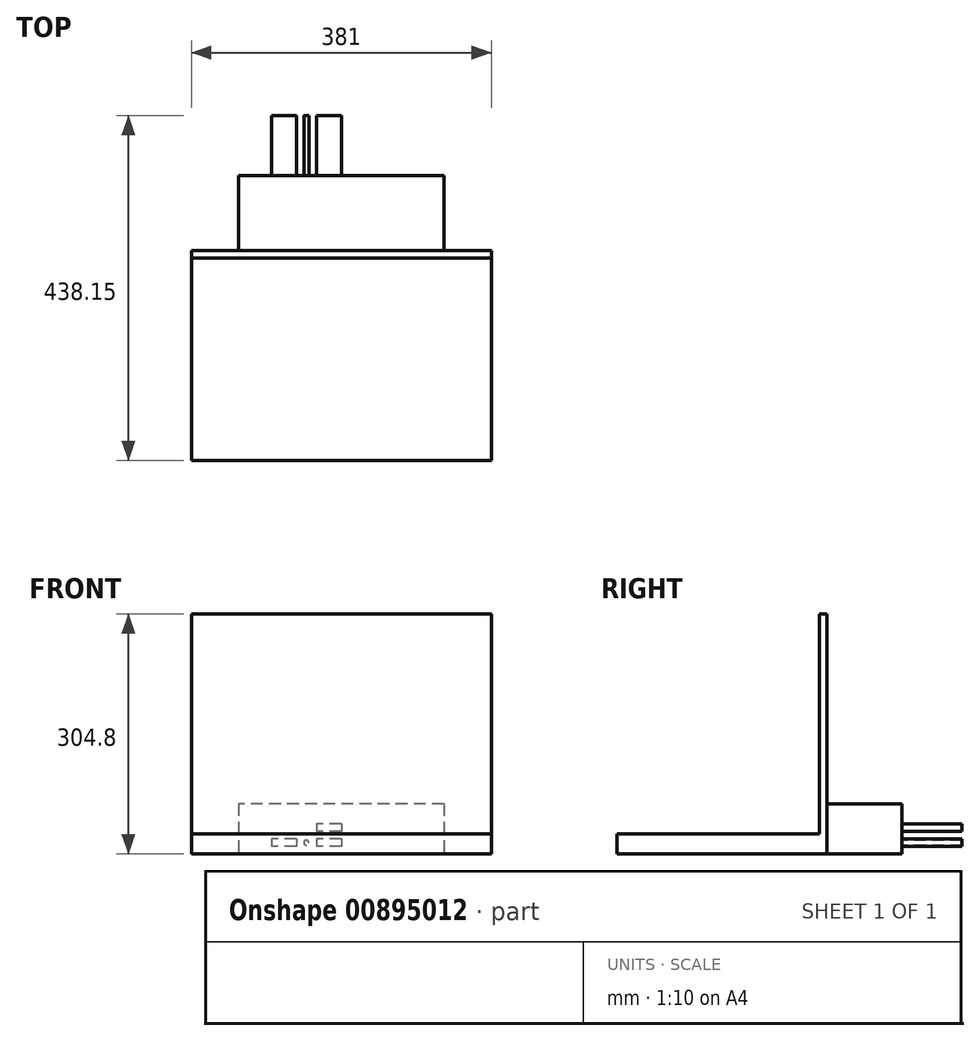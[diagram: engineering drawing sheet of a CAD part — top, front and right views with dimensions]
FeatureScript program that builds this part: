
annotation { "Feature Type Name" : "Feature", "Feature Type Description" : "" }
export const myFeature = defineFeature(function(context is Context, id is Id, definition is map)
    precondition{}
    {
        {
            var Q0;
            Q0=qCreatedBy(makeId("Right.planeOp"),FACE);
            var sketch = newSketch(context, id + "F0", { "sketchPlane" : qUnion([Q0])});
            skLineSegment(sketch, "E0", {"start": v(-266.7, 0) * mm, "end": v(0, 0) * mm});
            skLineSegment(sketch, "E1", {"start": v(0, 0) * mm, "end": v(0, 304.8) * mm});
            skLineSegment(sketch, "E2", {"start": v(0, 304.8) * mm, "end": v(-9.52, 304.8) * mm});
            skLineSegment(sketch, "E3", {"start": v(-9.52, 304.8) * mm, "end": v(-9.52, 25.4) * mm});
            skLineSegment(sketch, "E4", {"start": v(-9.52, 25.4) * mm, "end": v(-266.7, 25.4) * mm});
            skLineSegment(sketch, "E5", {"start": v(-266.7, 25.4) * mm, "end": v(-266.7, 0) * mm});
            skSolve(sketch);
        }
        {
            var Q0;
            Q0 = qSketchRegion(id + "F0", true);
            extrude(context, id + "F1", {"entities" : qUnion([Q0]), "depth" : 381 * mm, "offsetDistance" : 25.4 * mm, "symmetric" : true});
        }
        {
            var Q0;
            Q0=makeQuery(id+"F1.opExtrude","SWEPT_FACE",FACE,{"disambiguationData":[OSD([sQuery(id+"F0.wireOp",EDGE,"E1")])]});
            var sketch = newSketch(context, id + "F2", { "sketchPlane" : qUnion([Q0])});
            skLineSegment(sketch, "E6.bottom", {"start": v(-130.18, 63.5) * mm, "end": v(130.18, 63.5) * mm});
            skLineSegment(sketch, "E6.top", {"start": v(-130.17, 0) * mm, "end": v(130.18, 0) * mm});
            skLineSegment(sketch, "E6.left", {"start": v(-130.18, 63.5) * mm, "end": v(-130.18, 0) * mm});
            skLineSegment(sketch, "E6.right", {"start": v(130.18, 63.5) * mm, "end": v(130.18, 0) * mm});
            skSolve(sketch);
        }
        {
            var Q0;
            Q0 = qSketchRegion(id + "F2", true);
            extrude(context, id + "F3", {"entities" : qUnion([Q0]), "operationType" : NewBodyOperationType.ADD, "depth" : 95.25 * mm, "offsetDistance" : 25.4 * mm});
        }
        {
            var Q0;
            Q0=makeQuery(id+"F3.opExtrude","CAP_FACE",FACE,{"disambiguationData":[OSD([sQuery(id+"F2.wireOp",EDGE,"E6.bottom"),sQuery(id+"F2.wireOp",EDGE,"E6.top"),sQuery(id+"F2.wireOp",EDGE,"E6.left"),sQuery(id+"F2.wireOp",EDGE,"E6.right")])],"isStart":false});
            var sketch = newSketch(context, id + "F4", { "sketchPlane" : qUnion([Q0])});
            skLineSegment(sketch, "E7.bottom", {"start": v(0, 19.05) * mm, "end": v(31.75, 19.05) * mm});
            skLineSegment(sketch, "E7.top", {"start": v(0, 9.53) * mm, "end": v(31.75, 9.53) * mm});
            skLineSegment(sketch, "E7.left", {"start": v(0, 19.05) * mm, "end": v(0, 9.52) * mm});
            skLineSegment(sketch, "E7.right", {"start": v(31.75, 19.05) * mm, "end": v(31.75, 9.53) * mm});
            skLineSegment(sketch, "E8.bottom", {"start": v(57.15, 19.05) * mm, "end": v(88.9, 19.05) * mm});
            skLineSegment(sketch, "E8.top", {"start": v(57.15, 9.52) * mm, "end": v(88.9, 9.53) * mm});
            skLineSegment(sketch, "E8.left", {"start": v(57.15, 19.05) * mm, "end": v(57.15, 9.53) * mm});
            skLineSegment(sketch, "E8.right", {"start": v(88.9, 19.05) * mm, "end": v(88.9, 9.52) * mm});
            skLineSegment(sketch, "E9.bottom", {"start": v(0, 38.1) * mm, "end": v(31.75, 38.1) * mm});
            skLineSegment(sketch, "E9.top", {"start": v(0, 28.58) * mm, "end": v(31.75, 28.58) * mm});
            skLineSegment(sketch, "E9.left", {"start": v(0, 38.1) * mm, "end": v(0, 28.57) * mm});
            skLineSegment(sketch, "E9.right", {"start": v(31.75, 38.1) * mm, "end": v(31.75, 28.57) * mm});
            skCircle(sketch, "E10", {"center": v(44.45, 14.29) * mm, "radius": 3.18 * mm});
            skLineSegment(sketch, "E11", {"start": v(31.75, 14.29) * mm, "end": v(57.15, 14.29) * mm, "construction": true});
            skSolve(sketch);
        }
        {
            var Q0;
            Q0 = qSketchRegion(id + "F4", true);
            extrude(context, id + "F5", {"entities" : qUnion([Q0]), "operationType" : NewBodyOperationType.ADD, "depth" : 76.2 * mm, "offsetDistance" : 25.4 * mm});
        }
    });
